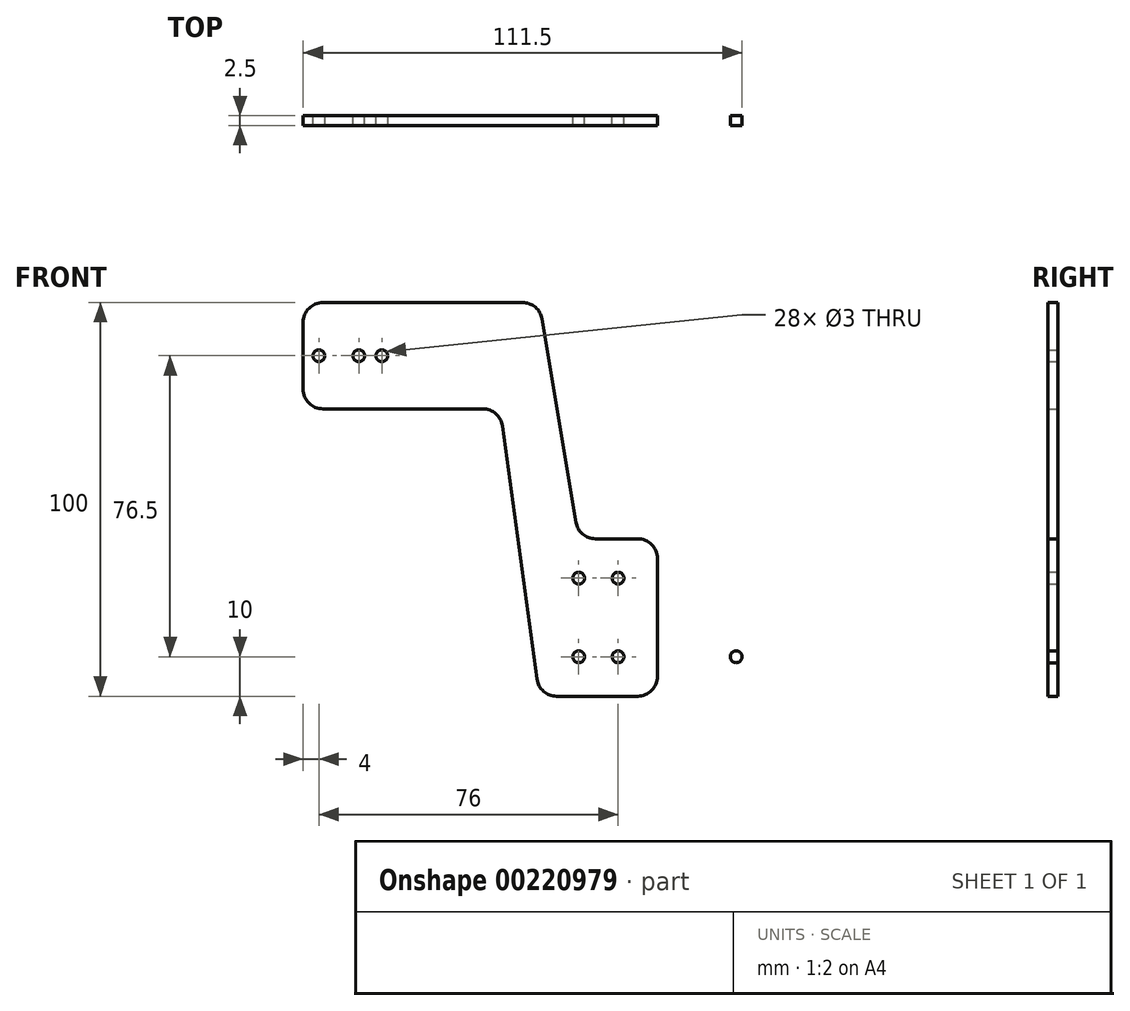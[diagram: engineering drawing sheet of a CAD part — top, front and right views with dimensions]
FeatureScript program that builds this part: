
annotation { "Feature Type Name" : "Feature", "Feature Type Description" : "" }
export const myFeature = defineFeature(function(context is Context, id is Id, definition is map)
    precondition{}
    {
        {
            var Q0;
            Q0=qCreatedBy(makeId("Front.planeOp"),FACE);
            var sketch = newSketch(context, id + "F0", { "sketchPlane" : qUnion([Q0])});
            skPoint(sketch, "E0.middle", {"position": v(0, 0) * mm});
            skLineSegment(sketch, "E1", {"start": v(0, -70) * mm, "end": v(0, -33.5) * mm});
            skPoint(sketch, "E1.endSnap0", {"position": v(0, -70) * mm});
            skLineSegment(sketch, "E2", {"start": v(0, -33.5) * mm, "end": v(0, -20) * mm});
            skCircle(sketch, "E3", {"center": v(-86, -33.5) * mm, "radius": 1.5 * mm});
            skCircle(sketch, "E4", {"center": v(-70, -33.5) * mm, "radius": 1.5 * mm});
            skLineSegment(sketch, "E5", {"start": v(-90, -33.5) * mm, "end": v(-90, -47) * mm});
            skLineSegment(sketch, "E6", {"start": v(-90, -20) * mm, "end": v(-30, -20) * mm});
            skLineSegment(sketch, "E7", {"start": v(-90, -47) * mm, "end": v(-40, -47) * mm});
            skLineSegment(sketch, "E8", {"start": v(0, -20) * mm, "end": v(0, -120) * mm});
            skLineSegment(sketch, "E9", {"start": v(0, -120) * mm, "end": v(0, -80) * mm});
            skPoint(sketch, "E9.endSnap0", {"position": v(0, -26.75) * mm});
            skLineSegment(sketch, "E10", {"start": v(0, -80) * mm, "end": v(-20, -80) * mm});
            skLineSegment(sketch, "E11", {"start": v(0, -120) * mm, "end": v(-30, -120) * mm});
            skLineSegment(sketch, "E12", {"start": v(-30, -120) * mm, "end": v(-40, -47) * mm});
            skLineSegment(sketch, "E13", {"start": v(-20, -80) * mm, "end": v(-30, -20) * mm});
            skCircle(sketch, "E14", {"center": v(-20, -110) * mm, "radius": 1.5 * mm});
            skCircle(sketch, "E15", {"center": v(-20, -90) * mm, "radius": 1.5 * mm});
            skLineSegment(sketch, "E16", {"start": v(-90, -33.5) * mm, "end": v(-90, -20) * mm});
            skCircle(sketch, "E17.MirrorC", {"center": v(20, -110) * mm, "radius": 1.5 * mm});
            skCircle(sketch, "E18.MirrorC", {"center": v(70, -33.5) * mm, "radius": 1.5 * mm});
            skCircle(sketch, "E19.MirrorC", {"center": v(86, -33.5) * mm, "radius": 1.5 * mm});
            skCircle(sketch, "E20.MirrorC", {"center": v(20, -90) * mm, "radius": 1.5 * mm});
            skLineSegment(sketch, "E21.MirrorCS", {"start": v(0, -80) * mm, "end": v(20, -80) * mm});
            skLineSegment(sketch, "E22.MirrorCS", {"start": v(90, -47) * mm, "end": v(40, -47) * mm});
            skLineSegment(sketch, "E23.MirrorCS", {"start": v(20, -80) * mm, "end": v(30, -20) * mm});
            skLineSegment(sketch, "E24.MirrorCS", {"start": v(0, -120) * mm, "end": v(30, -120) * mm});
            skLineSegment(sketch, "E25.MirrorCS", {"start": v(90, -33.5) * mm, "end": v(90, -20) * mm});
            skLineSegment(sketch, "E26.MirrorCS", {"start": v(90, -20) * mm, "end": v(30, -20) * mm});
            skLineSegment(sketch, "E27.MirrorCS", {"start": v(30, -120) * mm, "end": v(40, -47) * mm});
            skLineSegment(sketch, "E28.MirrorCS", {"start": v(90, -33.5) * mm, "end": v(90, -47) * mm});
            skCircle(sketch, "E29", {"center": v(-10, -90) * mm, "radius": 1.5 * mm});
            skCircle(sketch, "E30", {"center": v(-10, -110) * mm, "radius": 1.5 * mm});
            skCircle(sketch, "E31.MirrorC", {"center": v(10, -90) * mm, "radius": 1.5 * mm});
            skCircle(sketch, "E32.MirrorC", {"center": v(10, -110) * mm, "radius": 1.5 * mm});
            skCircle(sketch, "E33", {"center": v(-75.86, -33.5) * mm, "radius": 1.5 * mm});
            skCircle(sketch, "E34.MirrorC", {"center": v(75.86, -33.5) * mm, "radius": 1.5 * mm});
            skSolve(sketch);
        }
        {
            var Q0;
            {Q0=qUnion([makeQuery(id+"F0.imprint","IMPRINT",FACE,{"disambiguationData":[TD([[makeQuery(id+"F0.imprint","IMPRINT",EDGE,{"derivedFrom":sQuery(id+"F0.wireOp",EDGE,"E3")}),-1.0]])]}),makeQuery(id+"F0.imprint","IMPRINT",FACE,{"disambiguationData":[TD([[makeQuery(id+"F0.imprint","IMPRINT",EDGE,{"derivedFrom":sQuery(id+"F0.wireOp",EDGE,"E17.MirrorC")}),1.0]])]})]);}
            extrude(context, id + "F1", {"entities" : qUnion([Q0]), "depth" : 2.5 * mm});
        }
        {
            var Q0;
            Q0=makeQuery(id+"F1.opExtrude","SWEPT_EDGE",EDGE,{"disambiguationData":[OSD([sQuery(id+"F0.wireOp",EDGE,"E6"),sQuery(id+"F0.wireOp",EDGE,"E16")])]});
            var Q1;
            Q1=makeQuery(id+"F1.opExtrude","SWEPT_EDGE",EDGE,{"disambiguationData":[OSD([sQuery(id+"F0.wireOp",EDGE,"E5"),sQuery(id+"F0.wireOp",EDGE,"E7")])]});
            var Q2;
            Q2=makeQuery(id+"F1.opExtrude","SWEPT_EDGE",EDGE,{"disambiguationData":[OSD([sQuery(id+"F0.wireOp",EDGE,"E7"),sQuery(id+"F0.wireOp",EDGE,"E12")])]});
            var Q3;
            Q3=makeQuery(id+"F1.opExtrude","SWEPT_EDGE",EDGE,{"disambiguationData":[OSD([sQuery(id+"F0.wireOp",EDGE,"E11"),sQuery(id+"F0.wireOp",EDGE,"E12")])]});
            var Q4;
            Q4=makeQuery(id+"F1.opExtrude","SWEPT_EDGE",EDGE,{"disambiguationData":[OSD([sQuery(id+"F0.wireOp",EDGE,"E24.MirrorCS"),sQuery(id+"F0.wireOp",EDGE,"E27.MirrorCS")])]});
            var Q5;
            Q5=makeQuery(id+"F1.opExtrude","SWEPT_EDGE",EDGE,{"disambiguationData":[OSD([sQuery(id+"F0.wireOp",EDGE,"E22.MirrorCS"),sQuery(id+"F0.wireOp",EDGE,"E27.MirrorCS")])]});
            var Q6;
            Q6=makeQuery(id+"F1.opExtrude","SWEPT_EDGE",EDGE,{"disambiguationData":[OSD([sQuery(id+"F0.wireOp",EDGE,"E22.MirrorCS"),sQuery(id+"F0.wireOp",EDGE,"E28.MirrorCS")])]});
            var Q7;
            Q7=makeQuery(id+"F1.opExtrude","SWEPT_EDGE",EDGE,{"disambiguationData":[OSD([sQuery(id+"F0.wireOp",EDGE,"E6"),sQuery(id+"F0.wireOp",EDGE,"E13")])]});
            var Q8;
            Q8=makeQuery(id+"F1.opExtrude","SWEPT_EDGE",EDGE,{"disambiguationData":[OSD([sQuery(id+"F0.wireOp",EDGE,"E10"),sQuery(id+"F0.wireOp",EDGE,"E13")])]});
            var Q9;
            Q9=makeQuery(id+"F1.opExtrude","SWEPT_EDGE",EDGE,{"disambiguationData":[OSD([sQuery(id+"F0.wireOp",EDGE,"E23.MirrorCS"),sQuery(id+"F0.wireOp",EDGE,"E26.MirrorCS")])]});
            var Q10;
            Q10=makeQuery(id+"F1.opExtrude","SWEPT_EDGE",EDGE,{"disambiguationData":[OSD([sQuery(id+"F0.wireOp",EDGE,"E21.MirrorCS"),sQuery(id+"F0.wireOp",EDGE,"E23.MirrorCS")])]});
            var Q11;
            Q11=makeQuery(id+"F1.opExtrude","SWEPT_EDGE",EDGE,{"disambiguationData":[OSD([sQuery(id+"F0.wireOp",EDGE,"E25.MirrorCS"),sQuery(id+"F0.wireOp",EDGE,"E26.MirrorCS")])]});
            fillet(context, id + "F2", {"entities" : qUnion([Q0, Q1, Q2, Q3, Q4, Q5, Q6, Q7, Q8, Q9, Q10, Q11]), "radius" : 5 * mm, "tangentPropagation" : true, "allowEdgeOverflow" : false});
        }
    });
